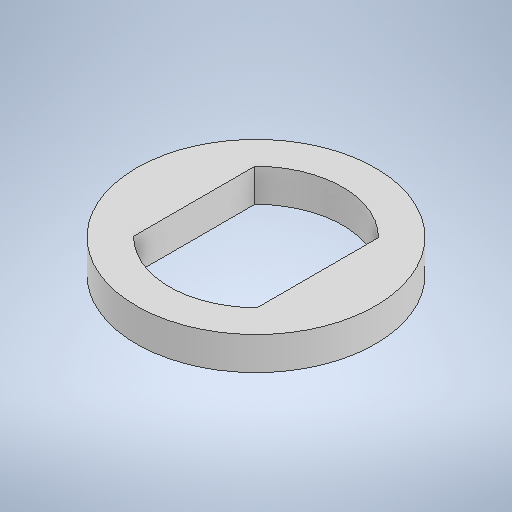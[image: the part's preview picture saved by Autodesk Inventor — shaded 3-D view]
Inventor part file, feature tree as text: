
AUTODESK INVENTOR PART (.ipt)
format: ipt  version: 2025.2 (Build 292293000, 293)  size: 248,832 bytes
history: native  units: mm
features: extrude x1, sketch x1
ambient origin geometry x8: Origin, YZ Plane, XZ Plane, XY Plane, X Axis, Y Axis, Z Axis, Center Point
bodies: Solid1 (feature_tree)
feature tree (2):
  extrude  "Extrusion1"  Depth=4.0mm
  sketch  "Sketch1"  dims[d0=29.0mm d1=21.0mm d2=7.0mm d3=7.0mm d4=4.0mm d5=0.0mm]
